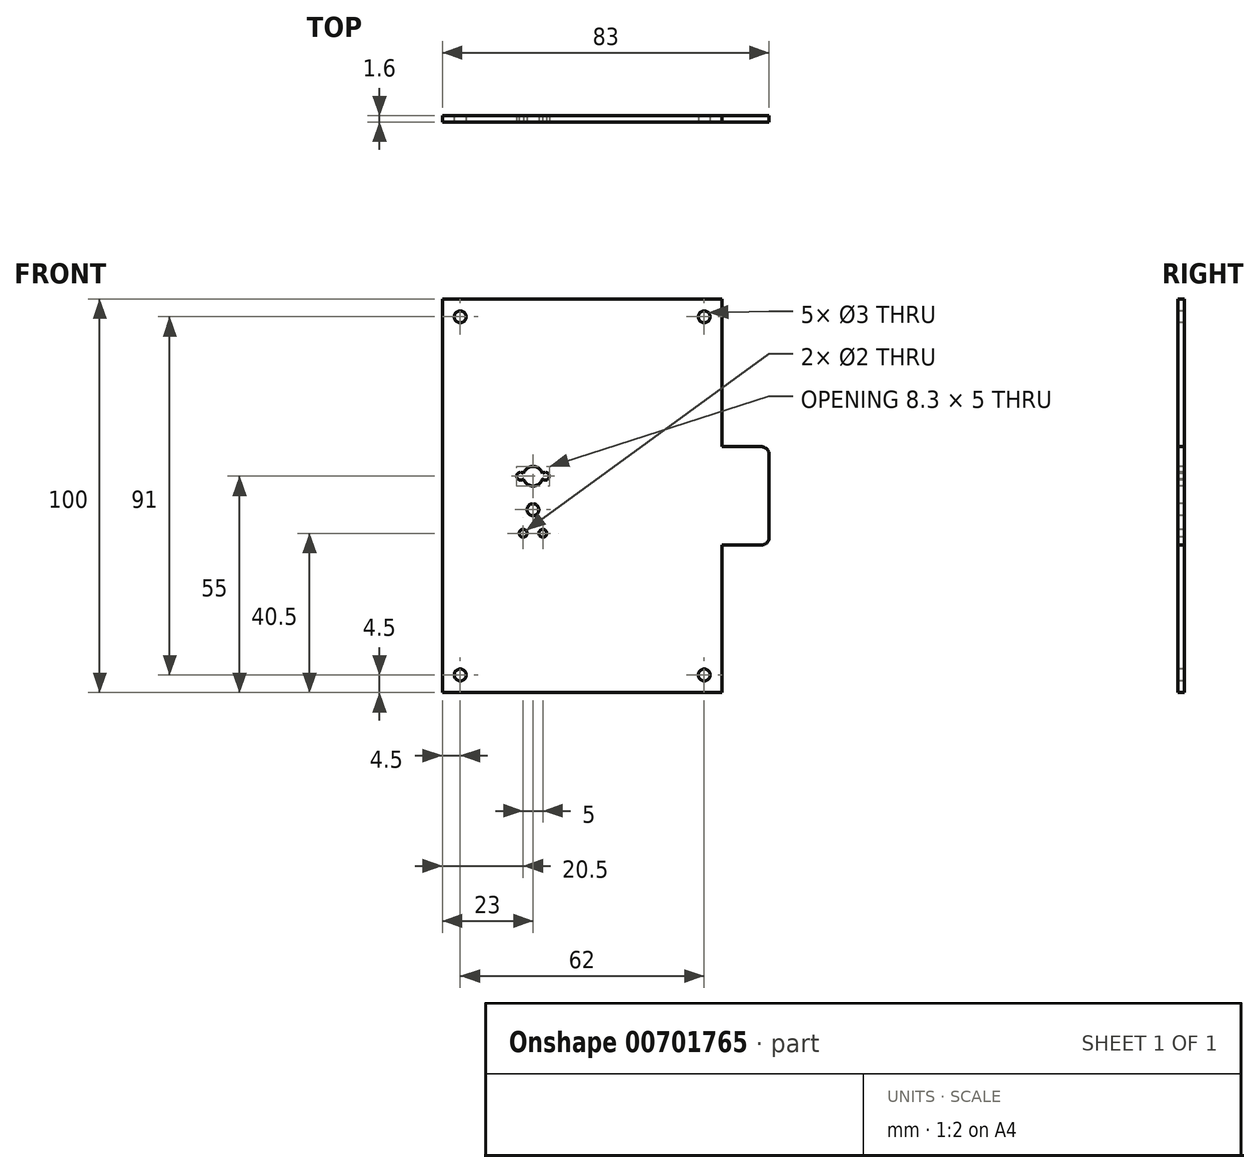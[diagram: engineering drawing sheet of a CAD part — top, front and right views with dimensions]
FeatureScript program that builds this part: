
annotation { "Feature Type Name" : "Feature", "Feature Type Description" : "" }
export const myFeature = defineFeature(function(context is Context, id is Id, definition is map)
    precondition{}
    {
        {
            var Q0;
            Q0=qCreatedBy(makeId("Front.planeOp"),FACE);
            var sketch = newSketch(context, id + "F0", { "sketchPlane" : qUnion([Q0])});
            skLineSegment(sketch, "E0.bottom", {"start": v(-35.5, 50) * mm, "end": v(35.5, 50) * mm});
            skLineSegment(sketch, "E0.top", {"start": v(-35.5, -50) * mm, "end": v(35.5, -50) * mm});
            skLineSegment(sketch, "E0.left", {"start": v(-35.5, 50) * mm, "end": v(-35.5, -50) * mm});
            skPoint(sketch, "E0.middle", {"position": v(0, 0) * mm});
            skCircle(sketch, "E1", {"center": v(-12.5, 5) * mm, "radius": 2.5 * mm});
            skCircle(sketch, "E2", {"center": v(-15.65, 5) * mm, "radius": 1 * mm});
            skLineSegment(sketch, "E3", {"start": v(-12.5, 5) * mm, "end": v(-12.5, 7.5) * mm});
            skCircle(sketch, "E4.MirrorC", {"center": v(-9.35, 5) * mm, "radius": 1 * mm});
            skLineSegment(sketch, "E5", {"start": v(35.5, 12.5) * mm, "end": v(45.5, 12.5) * mm});
            skLineSegment(sketch, "E6", {"start": v(47.5, 10.5) * mm, "end": v(47.5, -10.5) * mm});
            skLineSegment(sketch, "E7", {"start": v(45.5, -12.5) * mm, "end": v(35.5, -12.5) * mm});
            skLineSegment(sketch, "E8", {"start": v(35.5, -12.5) * mm, "end": v(35.5, -50) * mm});
            skLineSegment(sketch, "E9", {"start": v(35.5, 12.5) * mm, "end": v(35.5, 50) * mm});
            skLineSegment(sketch, "E10", {"start": v(1.41, 0) * mm, "end": v(47.5, 0) * mm, "construction": true});
            skPoint(sketch, "E11.visualSharp", {"position": v(47.5, 12.5) * mm});
            skArc(sketch, "E11.filletArc", {"start": v(47.5, 10.5) * mm, "mid": v(46.91, 11.91) * mm, "end": v(45.5, 12.5) * mm});
            skPoint(sketch, "E12.visualSharp", {"position": v(47.5, -12.5) * mm});
            skArc(sketch, "E12.filletArc", {"start": v(45.5, -12.5) * mm, "mid": v(46.91, -11.91) * mm, "end": v(47.5, -10.5) * mm});
            skCircle(sketch, "E13", {"center": v(-31, 45.5) * mm, "radius": 1.5 * mm});
            skCircle(sketch, "E14", {"center": v(31, 45.5) * mm, "radius": 1.5 * mm});
            skCircle(sketch, "E15", {"center": v(-31, -45.5) * mm, "radius": 1.5 * mm});
            skCircle(sketch, "E16", {"center": v(31, -45.5) * mm, "radius": 1.5 * mm});
            skLineSegment(sketch, "E17.bottom", {"start": v(-35.5, 35) * mm, "end": v(-37.5, 35) * mm, "construction": true});
            skLineSegment(sketch, "E17.top", {"start": v(-35.5, -27) * mm, "end": v(-37.5, -27) * mm, "construction": true});
            skLineSegment(sketch, "E17.left", {"start": v(-35.5, 35) * mm, "end": v(-35.5, -27) * mm});
            skLineSegment(sketch, "E17.right", {"start": v(-37.5, 35) * mm, "end": v(-37.5, -27) * mm, "construction": true});
            skPoint(sketch, "E18", {"position": v(-37.5, 4) * mm});
            skCircle(sketch, "E19", {"center": v(-12.5, -3.5) * mm, "radius": 1.5 * mm});
            skLineSegment(sketch, "E20", {"start": v(-12.5, 5) * mm, "end": v(-12.5, -50) * mm, "construction": true});
            skCircle(sketch, "E21", {"center": v(-15, -9.5) * mm, "radius": 1 * mm});
            skCircle(sketch, "E22", {"center": v(-10, -9.5) * mm, "radius": 1 * mm});
            skSolve(sketch);
        }
        {
            var Q0;
            Q0=makeQuery(id+"F0.imprint","IMPRINT",FACE,{"disambiguationData":[TD([[makeQuery(id+"F0.imprint","IMPRINT",EDGE,{"derivedFrom":sQuery(id+"F0.wireOp",EDGE,"E0.bottom")}),-1.0]])]});
            var Q1;
            Q1=makeQuery(id+"F0.imprint","IMPRINT",FACE,{"disambiguationData":[TD([[makeQuery(id+"F0.imprint","IMPRINT",EDGE,{"derivedFrom":sQuery(id+"F0.wireOp",EDGE,"E17.bottom")}),1.0]])]});
            extrude(context, id + "F1", {"entities" : qUnion([Q0, Q1]), "oppositeDirection" : true, "depth" : 1.6 * mm});
        }
        {
            var Q0;
            Q0=makeQuery(id+"F1.opExtrude","SWEPT_FACE",FACE,{"disambiguationData":[OSD([sQuery(id+"F0.wireOp",EDGE,"E6")])]});
            var sketch = newSketch(context, id + "F2", { "sketchPlane" : qUnion([Q0])});
            skLineSegment(sketch, "E23", {"start": v(0, 0) * mm, "end": v(1.6, 0) * mm, "construction": true});
            skPoint(sketch, "E24", {"position": v(0.8, 0) * mm});
            skSolve(sketch);
        }
    });
